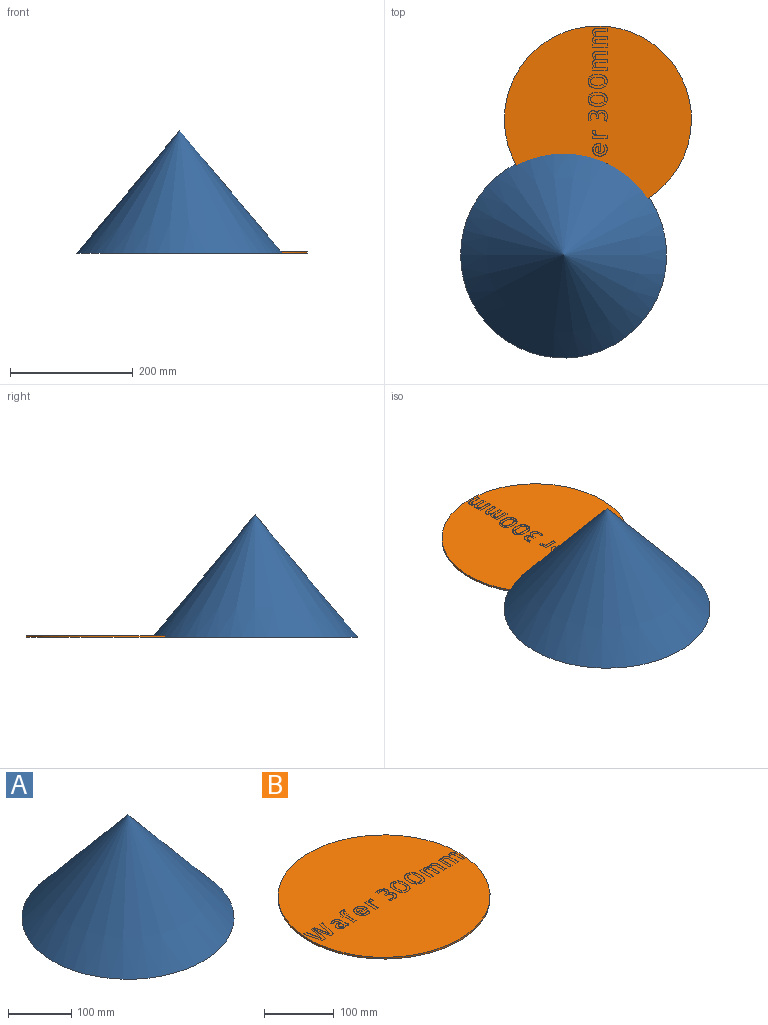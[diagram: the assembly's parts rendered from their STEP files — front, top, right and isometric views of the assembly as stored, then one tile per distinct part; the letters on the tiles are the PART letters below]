
ASSEMBLY  parts=2 mates=1
PART A: 2 faces, bbox 335.6x335.6x200 mm
  f0: plane 335.64x335.64mm, normal (0,0,-1), area 88478.3mm2, adj f1
  f1: cone r=0mm half-angle=40deg, axis (0,0,-1), area 137647.8mm2, adj f0
PART B: 355 faces, bbox 304.8x304.8x3 mm
  f0: plane 304.8x304.8mm, normal (0,0,1), area 70013.2mm2, adj f1,f3,f4,f5,f6,f7,f9,f10
  f1: cylinder r=152.4mm len=304.8mm, axis (0,0,1), area 2872.7mm2, adj f0,f2
  f2: plane 304.8x304.8mm, normal (0,0,-1), area 72965.9mm2, adj f1
  f3: plane 4.49x0.5mm, normal (0,-1,0), area 2.2mm2, adj f0,f4,f7,f8
  f4: plane 23.22x0.5mm, normal (1,0,0), area 11.6mm2, adj f0,f3,f5,f8
  f5: plane 5.02x0.5mm, normal (0,1,0), area 2.5mm2, adj f0,f4,f6,f8
  f6: plane 20.84x0.5mm, normal (-1,0,0), area 10.4mm2, adj f0,f5,f7,f8
  f7: plane 2.38x0.53mm, normal (-0.98,-0.22,0), area 1.2mm2, adj f0,f3,f6,f8
  f8: plane 23.22x5.02mm, normal (0,0,1), area 115.9mm2, adj f3,f4,f5,f6,f7
  f9: extruded ~2.14x0.5mm, area 1.1mm2, adj f0,f10,f24,f25
  f10: extruded ~2.27x1.03mm, area 1.2mm2, adj f0,f9,f11,f25
  f11: plane 3.25x0.5mm, normal (1,0,0), area 1.6mm2, adj f0,f10,f12,f25
  f12: extruded ~2.18x0.7mm, area 1.2mm2, adj f0,f11,f13,f25
  f13: extruded ~1.24x0.5mm, area 0.6mm2, adj f0,f12,f14,f25
  f14: extruded ~1.71x0.55mm, area 0.9mm2, adj f0,f13,f15,f25
  f15: extruded ~1.54x0.8mm, area 0.9mm2, adj f0,f14,f16,f25
  f16: extruded ~2.25x0.5mm, area 1.1mm2, adj f0,f15,f17,f25
  f17: extruded ~2.65x0.5mm, area 1.3mm2, adj f0,f16,f18,f25
  f18: plane 12.64x0.5mm, normal (1,0,0), area 6.3mm2, adj f0,f17,f19,f25
  f19: plane 4.94x0.5mm, normal (0,1,0), area 2.5mm2, adj f0,f18,f20,f25
  f20: plane 15.81x0.5mm, normal (-1,0,0), area 7.9mm2, adj f0,f19,f21,f25
  f21: extruded ~3.07x0.51mm, area 1.6mm2, adj f0,f20,f22,f25
  f22: extruded ~2.45x1.44mm, area 1.4mm2, adj f0,f21,f23,f25
  f23: extruded ~2.16x1.59mm, area 1.4mm2, adj f0,f22,f24,f25
  f24: extruded ~2.63x0.56mm, area 1.4mm2, adj f0,f9,f23,f25
  f25: plane 23.47x11.16mm, normal (0,0,1), area 130mm2, adj f9,f10,f11,f12,f13,f14,f15,f16
  f26: extruded ~2.54x2.31mm, area 1.7mm2, adj f0,f27,f43,f44
  f27: extruded ~3.19x0.78mm, area 1.7mm2, adj f0,f26,f28,f44
  f28: extruded ~2.25x0.5mm, area 1.1mm2, adj f0,f27,f29,f44
  f29: extruded ~2.12x0.95mm, area 1.2mm2, adj f0,f28,f30,f44
  f30: plane 3.25x0.5mm, normal (1,0,0), area 1.6mm2, adj f0,f29,f31,f44
  f31: extruded ~1.92x0.64mm, area 1mm2, adj f0,f30,f32,f44
  f32: extruded ~1.46x0.5mm, area 0.7mm2, adj f0,f31,f33,f44
  f33: extruded ~1.69x0.55mm, area 0.9mm2, adj f0,f32,f34,f44
  f34: extruded ~1.54x0.82mm, area 0.9mm2, adj f0,f33,f35,f44
  f35: extruded ~2.25x0.5mm, area 1.1mm2, adj f0,f34,f36,f44
  f36: plane 2.65x0.5mm, normal (1,0,0), area 1.3mm2, adj f0,f35,f37,f44
  f37: plane 12.64x0.5mm, normal (1,0,0), area 6.3mm2, adj f0,f36,f38,f44
  f38: plane 4.98x0.5mm, normal (0,1,0), area 2.5mm2, adj f0,f37,f39,f44
  f39: plane 13.05x0.5mm, normal (-1,0,0), area 6.5mm2, adj f0,f38,f40,f44
  f40: extruded ~2.04x0.5mm, area 1mm2, adj f0,f39,f41,f44
  f41: extruded ~1.87x0.5mm, area 0.9mm2, adj f0,f40,f42,f44
  f42: extruded ~1.75x0.5mm, area 0.9mm2, adj f0,f41,f43,f44
  f43: extruded ~1.58x0.72mm, area 0.9mm2, adj f0,f26,f42,f44
  f44: plane 23.38x11.15mm, normal (0,0,1), area 130.7mm2, adj f26,f27,f28,f29,f30,f31,f32,f33
  f45: extruded ~3.04x0.87mm, area 1.6mm2, adj f0,f46,f60,f61
  f46: plane 3.87x1.81mm, normal (-0.91,0.42,0), area 2.1mm2, adj f0,f45,f47,f61
  f47: extruded ~4.98x1.07mm, area 2.6mm2, adj f0,f46,f48,f61
  f48: extruded ~4.84x1.01mm, area 2.5mm2, adj f0,f47,f49,f61
  f49: extruded ~3.67x2.94mm, area 2.4mm2, adj f0,f48,f50,f61
  f50: extruded ~4.84x2.31mm, area 2.7mm2, adj f0,f49,f51,f61
  f51: extruded ~6.73x0.8mm, area 3.4mm2, adj f0,f50,f52,f61
  f52: extruded ~7.51x1.03mm, area 3.8mm2, adj f0,f51,f53,f61
  f53: extruded ~5.04x2.92mm, area 2.9mm2, adj f0,f52,f54,f61
  f54: plane 4.82x2.26mm, normal (-0.91,0.42,0), area 2.7mm2, adj f0,f53,f55,f61
  f55: extruded ~3.29x0.86mm, area 1.7mm2, adj f0,f54,f56,f61
  f56: extruded ~4.45x0.5mm, area 2.2mm2, adj f0,f55,f57,f61
  f57: extruded ~5.35x0.51mm, area 2.7mm2, adj f0,f56,f58,f61
  f58: extruded ~3.56x1.34mm, area 1.9mm2, adj f0,f57,f59,f61
  f59: extruded ~2.1x1.96mm, area 1.5mm2, adj f0,f58,f60,f61
  f60: extruded ~2.76x0.58mm, area 1.4mm2, adj f0,f45,f59,f61
  f61: plane 28.07x16.59mm, normal (0,0,1), area 155.3mm2, adj f45,f46,f47,f48,f49,f50,f51,f52
  f62: plane 4.78x2.27mm, normal (0.9,-0.43,0), area 2.6mm2, adj f0,f63,f78,f79
  f63: extruded ~0.5x0.08mm, area 0mm2, adj f0,f62,f64,f79
  f64: extruded ~3.3x0.95mm, area 1.7mm2, adj f0,f63,f65,f79
  f65: extruded ~4.53x0.5mm, area 2.3mm2, adj f0,f64,f66,f79
  f66: extruded ~5.37x0.51mm, area 2.7mm2, adj f0,f65,f67,f79
  f67: extruded ~3.56x1.34mm, area 1.9mm2, adj f0,f66,f68,f79
  f68: extruded ~2.12x1.96mm, area 1.5mm2, adj f0,f67,f69,f79
  f69: extruded ~2.78x0.6mm, area 1.4mm2, adj f0,f68,f70,f79
  f70: extruded ~3.21x1.03mm, area 1.7mm2, adj f0,f69,f71,f79
  f71: plane 3.91x1.85mm, normal (0.9,-0.43,0), area 2.2mm2, adj f0,f70,f72,f79
  f72: extruded ~5.18x1.15mm, area 2.7mm2, adj f0,f71,f73,f79
  f73: extruded ~4.86x0.99mm, area 2.5mm2, adj f0,f72,f74,f79
  f74: extruded ~3.66x2.92mm, area 2.4mm2, adj f0,f73,f75,f79
  f75: extruded ~4.86x2.33mm, area 2.7mm2, adj f0,f74,f76,f79
  f76: extruded ~6.75x0.8mm, area 3.4mm2, adj f0,f75,f77,f79
  f77: extruded ~7.62x1.05mm, area 3.9mm2, adj f0,f76,f78,f79
  f78: extruded ~5.06x3.07mm, area 3mm2, adj f0,f62,f77,f79
  f79: plane 28.2x16.84mm, normal (0,0,1), area 157.8mm2, adj f62,f63,f64,f65,f66,f67,f68,f69
  f80: extruded ~3.04x0.87mm, area 1.6mm2, adj f0,f81,f95,f96
  f81: plane 3.87x1.81mm, normal (-0.91,0.42,0), area 2.1mm2, adj f0,f80,f82,f96
  f82: extruded ~4.98x1.07mm, area 2.6mm2, adj f0,f81,f83,f96
  f83: extruded ~4.84x1.01mm, area 2.5mm2, adj f0,f82,f84,f96
  f84: extruded ~3.67x2.94mm, area 2.4mm2, adj f0,f83,f85,f96
  f85: extruded ~4.84x2.31mm, area 2.7mm2, adj f0,f84,f86,f96
  f86: extruded ~6.73x0.8mm, area 3.4mm2, adj f0,f85,f87,f96
  f87: extruded ~7.51x1.03mm, area 3.8mm2, adj f0,f86,f88,f96
  f88: extruded ~5.04x2.92mm, area 2.9mm2, adj f0,f87,f89,f96
  f89: plane 4.82x2.26mm, normal (-0.91,0.42,0), area 2.7mm2, adj f0,f88,f90,f96
  f90: extruded ~3.29x0.86mm, area 1.7mm2, adj f0,f89,f91,f96
  f91: extruded ~4.45x0.5mm, area 2.2mm2, adj f0,f90,f92,f96
  f92: extruded ~5.35x0.51mm, area 2.7mm2, adj f0,f91,f93,f96
  f93: extruded ~3.56x1.34mm, area 1.9mm2, adj f0,f92,f94,f96
  f94: extruded ~2.1x1.96mm, area 1.5mm2, adj f0,f93,f95,f96
  f95: extruded ~2.76x0.58mm, area 1.4mm2, adj f0,f80,f94,f96
  f96: plane 28.07x16.59mm, normal (0,0,1), area 155.3mm2, adj f80,f81,f82,f83,f84,f85,f86,f87
  f97: plane 3.34x0.5mm, normal (1,0.01,0), area 1.7mm2, adj f0,f98,f141,f142
  f98: plane 4.16x0.5mm, normal (0,1,0), area 2.1mm2, adj f0,f97,f99,f142
  f99: extruded ~3.75x1.52mm, area 2.1mm2, adj f0,f98,f100,f142
  f100: extruded ~3.75x1.28mm, area 2mm2, adj f0,f99,f101,f142
  f101: extruded ~3.89x1.4mm, area 2.1mm2, adj f0,f100,f102,f142
  f102: extruded ~4.25x1.54mm, area 2.3mm2, adj f0,f101,f103,f142
  f103: extruded ~3.04x0.5mm, area 1.5mm2, adj f0,f102,f104,f142
  f104: extruded ~1.73x0.5mm, area 0.9mm2, adj f0,f103,f105,f142
  f105: extruded ~0.95x0.5mm, area 0.5mm2, adj f0,f104,f106,f142
  f106: extruded ~0.71x0.5mm, area 0.4mm2, adj f0,f105,f107,f142
  f107: plane 3.54x1.11mm, normal (0.95,-0.3,0), area 1.9mm2, adj f0,f106,f108,f142
  f108: extruded ~2.78x0.97mm, area 1.5mm2, adj f0,f107,f109,f142
  f109: extruded ~5.46x0.5mm, area 2.7mm2, adj f0,f108,f110,f142
  f110: extruded ~1.38x0.5mm, area 0.7mm2, adj f0,f109,f111,f142
  f111: extruded ~1.95x0.5mm, area 1mm2, adj f0,f110,f112,f142
  f112: extruded ~2.2x0.89mm, area 1.2mm2, adj f0,f111,f113,f142
  f113: extruded ~2.04x1.59mm, area 1.3mm2, adj f0,f112,f114,f142
  f114: extruded ~2.49x1.5mm, area 1.5mm2, adj f0,f113,f115,f142
  f115: extruded ~3.56x0.6mm, area 1.8mm2, adj f0,f114,f116,f142
  f116: extruded ~2.99x0.58mm, area 1.5mm2, adj f0,f115,f117,f142
  f117: extruded ~2.2x1.44mm, area 1.3mm2, adj f0,f116,f118,f142
  f118: extruded ~1.87x1.4mm, area 1.2mm2, adj f0,f117,f119,f142
  f119: extruded ~1.96x0.62mm, area 1mm2, adj f0,f118,f120,f142
  f120: extruded ~1.6x0.68mm, area 0.9mm2, adj f0,f119,f121,f142
  f121: extruded ~1.56x1.3mm, area 1mm2, adj f0,f120,f122,f142
  f122: extruded ~1.83x1.15mm, area 1.1mm2, adj f0,f121,f123,f142
  f123: extruded ~2.32x0.5mm, area 1.2mm2, adj f0,f122,f124,f142
  f124: extruded ~3.79x0.76mm, area 1.9mm2, adj f0,f123,f125,f142
  f125: extruded ~2.64x2.06mm, area 1.7mm2, adj f0,f124,f126,f142
  f126: extruded ~3.03x1.5mm, area 1.7mm2, adj f0,f125,f127,f142
  f127: extruded ~3.67x0.5mm, area 1.9mm2, adj f0,f126,f128,f142
  f128: extruded ~4.22x0.5mm, area 2.1mm2, adj f0,f127,f129,f142
  f129: extruded ~2.45x0.61mm, area 1.3mm2, adj f0,f128,f130,f142
  f130: plane 3.71x1.44mm, normal (0.93,0.36,0), area 2mm2, adj f0,f129,f131,f142
  f131: extruded ~1.71x0.56mm, area 0.9mm2, adj f0,f130,f132,f142
  f132: extruded ~3.02x0.5mm, area 1.5mm2, adj f0,f131,f133,f142
  f133: extruded ~2.97x0.5mm, area 1.5mm2, adj f0,f132,f134,f142
  f134: extruded ~1.62x1.13mm, area 1mm2, adj f0,f133,f135,f142
  f135: extruded ~1.52x0.68mm, area 0.8mm2, adj f0,f134,f136,f142
  f136: extruded ~1.57x0.5mm, area 0.8mm2, adj f0,f135,f137,f142
  f137: extruded ~2.84x0.54mm, area 1.5mm2, adj f0,f136,f138,f142
  f138: extruded ~1.4x1.36mm, area 1mm2, adj f0,f137,f139,f142
  f139: extruded ~1.75x0.5mm, area 0.9mm2, adj f0,f138,f140,f142
  f140: extruded ~1.83x0.5mm, area 0.9mm2, adj f0,f139,f141,f142
  f141: plane 2.8x0.5mm, normal (0,-1,0), area 1.4mm2, adj f0,f97,f140,f142
  f142: plane 30.71x17.9mm, normal (0,0,1), area 228.3mm2, adj f97,f98,f99,f100,f101,f102,f103,f104
  f143: plane 4.78x2.27mm, normal (0.9,-0.43,0), area 2.6mm2, adj f0,f144,f159,f160
  f144: extruded ~0.5x0.08mm, area 0mm2, adj f0,f143,f145,f160
  f145: extruded ~3.3x0.95mm, area 1.7mm2, adj f0,f144,f146,f160
  f146: extruded ~4.53x0.5mm, area 2.3mm2, adj f0,f145,f147,f160
  f147: extruded ~5.37x0.51mm, area 2.7mm2, adj f0,f146,f148,f160
  f148: extruded ~3.56x1.34mm, area 1.9mm2, adj f0,f147,f149,f160
  f149: extruded ~2.12x1.96mm, area 1.5mm2, adj f0,f148,f150,f160
  f150: extruded ~2.78x0.6mm, area 1.4mm2, adj f0,f149,f151,f160
  f151: extruded ~3.21x1.03mm, area 1.7mm2, adj f0,f150,f152,f160
  f152: plane 3.91x1.85mm, normal (0.9,-0.43,0), area 2.2mm2, adj f0,f151,f153,f160
  f153: extruded ~5.18x1.15mm, area 2.7mm2, adj f0,f152,f154,f160
  f154: extruded ~4.86x0.99mm, area 2.5mm2, adj f0,f153,f155,f160
  f155: extruded ~3.66x2.92mm, area 2.4mm2, adj f0,f154,f156,f160
  f156: extruded ~4.86x2.33mm, area 2.7mm2, adj f0,f155,f157,f160
  f157: extruded ~6.75x0.8mm, area 3.4mm2, adj f0,f156,f158,f160
  f158: extruded ~7.62x1.05mm, area 3.9mm2, adj f0,f157,f159,f160
  f159: extruded ~5.06x3.07mm, area 3mm2, adj f0,f143,f158,f160
  f160: plane 28.2x16.84mm, normal (0,0,1), area 157.8mm2, adj f143,f144,f145,f146,f147,f148,f149,f150
  f161: plane 4.49x0.5mm, normal (0,-1,0), area 2.2mm2, adj f0,f162,f165,f166
  f162: plane 23.22x0.5mm, normal (1,0,0), area 11.6mm2, adj f0,f161,f163,f166
  f163: plane 5.02x0.5mm, normal (0,1,0), area 2.5mm2, adj f0,f162,f164,f166
  f164: plane 20.84x0.5mm, normal (-1,0,0), area 10.4mm2, adj f0,f163,f165,f166
  f165: plane 2.38x0.53mm, normal (-0.98,-0.22,0), area 1.2mm2, adj f0,f161,f164,f166
  f166: plane 23.22x5.02mm, normal (0,0,1), area 115.9mm2, adj f161,f162,f163,f164,f165
  f167: extruded ~2.14x0.5mm, area 1.1mm2, adj f0,f168,f182,f183
  f168: extruded ~2.27x1.03mm, area 1.2mm2, adj f0,f167,f169,f183
  f169: plane 3.25x0.5mm, normal (1,0,0), area 1.6mm2, adj f0,f168,f170,f183
  f170: extruded ~2.18x0.7mm, area 1.2mm2, adj f0,f169,f171,f183
  f171: extruded ~1.24x0.5mm, area 0.6mm2, adj f0,f170,f172,f183
  f172: extruded ~1.71x0.55mm, area 0.9mm2, adj f0,f171,f173,f183
  f173: extruded ~1.54x0.8mm, area 0.9mm2, adj f0,f172,f174,f183
  f174: extruded ~2.25x0.5mm, area 1.1mm2, adj f0,f173,f175,f183
  f175: extruded ~2.65x0.5mm, area 1.3mm2, adj f0,f174,f176,f183
  f176: plane 12.64x0.5mm, normal (1,0,0), area 6.3mm2, adj f0,f175,f177,f183
  f177: plane 4.94x0.5mm, normal (0,1,0), area 2.5mm2, adj f0,f176,f178,f183
  f178: plane 15.81x0.5mm, normal (-1,0,0), area 7.9mm2, adj f0,f177,f179,f183
  f179: extruded ~3.07x0.51mm, area 1.6mm2, adj f0,f178,f180,f183
  f180: extruded ~2.45x1.44mm, area 1.4mm2, adj f0,f179,f181,f183
  f181: extruded ~2.16x1.59mm, area 1.4mm2, adj f0,f180,f182,f183
  f182: extruded ~2.63x0.56mm, area 1.4mm2, adj f0,f167,f181,f183
  f183: plane 23.47x11.16mm, normal (0,0,1), area 130mm2, adj f167,f168,f169,f170,f171,f172,f173,f174
  f184: extruded ~2.54x2.31mm, area 1.7mm2, adj f0,f185,f201,f202
  f185: extruded ~3.19x0.78mm, area 1.7mm2, adj f0,f184,f186,f202
  f186: extruded ~2.25x0.5mm, area 1.1mm2, adj f0,f185,f187,f202
  f187: extruded ~2.12x0.95mm, area 1.2mm2, adj f0,f186,f188,f202
  f188: plane 3.25x0.5mm, normal (1,0,0), area 1.6mm2, adj f0,f187,f189,f202
  f189: extruded ~1.92x0.64mm, area 1mm2, adj f0,f188,f190,f202
  f190: extruded ~1.46x0.5mm, area 0.7mm2, adj f0,f189,f191,f202
  f191: extruded ~1.69x0.55mm, area 0.9mm2, adj f0,f190,f192,f202
  f192: extruded ~1.54x0.82mm, area 0.9mm2, adj f0,f191,f193,f202
  f193: extruded ~2.25x0.5mm, area 1.1mm2, adj f0,f192,f194,f202
  f194: plane 2.65x0.5mm, normal (1,0,0), area 1.3mm2, adj f0,f193,f195,f202
  f195: plane 12.64x0.5mm, normal (1,0,0), area 6.3mm2, adj f0,f194,f196,f202
  f196: plane 4.98x0.5mm, normal (0,1,0), area 2.5mm2, adj f0,f195,f197,f202
  f197: plane 13.05x0.5mm, normal (-1,0,0), area 6.5mm2, adj f0,f196,f198,f202
  f198: extruded ~2.04x0.5mm, area 1mm2, adj f0,f197,f199,f202
  f199: extruded ~1.87x0.5mm, area 0.9mm2, adj f0,f198,f200,f202
  f200: extruded ~1.75x0.5mm, area 0.9mm2, adj f0,f199,f201,f202
  f201: extruded ~1.58x0.72mm, area 0.9mm2, adj f0,f184,f200,f202
  f202: plane 23.38x11.15mm, normal (0,0,1), area 130.7mm2, adj f184,f185,f186,f187,f188,f189,f190,f191
  f203: plane 4.2x0.5mm, normal (1,0,0), area 2.1mm2, adj f0,f204,f209,f210
  f204: extruded ~1.75x0.5mm, area 0.9mm2, adj f0,f203,f205,f210
  f205: extruded ~1.83x0.5mm, area 0.9mm2, adj f0,f204,f206,f210
  f206: extruded ~2.8x0.5mm, area 1.4mm2, adj f0,f205,f207,f210
  f207: plane 5.18x0.5mm, normal (-1,0,0), area 2.6mm2, adj f0,f206,f208,f210
  f208: extruded ~3.91x0.5mm, area 2mm2, adj f0,f207,f209,f210
  f209: extruded ~2.47x0.88mm, area 1.3mm2, adj f0,f203,f208,f210
  f210: plane 6.38x5.4mm, normal (0,0,1), area 29.7mm2, adj f203,f204,f205,f206,f207,f208,f209
  f211: plane 4.45x0.5mm, normal (0,-1,0), area 2.2mm2, adj f0,f212,f215,f216
  f212: plane 23.22x0.5mm, normal (1,0,0), area 11.6mm2, adj f0,f211,f213,f216
  f213: plane 4.98x0.5mm, normal (0,1,0), area 2.5mm2, adj f0,f212,f214,f216
  f214: plane 20.84x0.5mm, normal (-1,0,0), area 10.4mm2, adj f0,f213,f215,f216
  f215: plane 2.38x0.53mm, normal (-0.98,-0.22,0), area 1.2mm2, adj f0,f211,f214,f216
  f216: plane 23.22x4.98mm, normal (0,0,1), area 115mm2, adj f211,f212,f213,f214,f215
  f217: plane 3.87x0.5mm, normal (1,0,0), area 1.9mm2, adj f0,f218,f229,f230
  f218: extruded ~2.02x0.7mm, area 1.1mm2, adj f0,f217,f219,f230
  f219: extruded ~1.58x1.42mm, area 1.1mm2, adj f0,f218,f220,f230
  f220: extruded ~1.83x1.03mm, area 1.1mm2, adj f0,f219,f221,f230
  f221: extruded ~2.06x0.5mm, area 1.1mm2, adj f0,f220,f222,f230
  f222: plane 9.51x0.5mm, normal (0,-1,0), area 4.8mm2, adj f0,f221,f223,f230
  f223: plane 3.62x0.5mm, normal (1,0,0), area 1.8mm2, adj f0,f222,f224,f230
  f224: plane 14.12x0.5mm, normal (0,1,0), area 7.1mm2, adj f0,f223,f225,f230
  f225: extruded ~1.98x0.5mm, area 1mm2, adj f0,f224,f226,f230
  f226: extruded ~4.2x0.68mm, area 2.1mm2, adj f0,f225,f227,f230
  f227: extruded ~3.58x1.96mm, area 2.1mm2, adj f0,f226,f228,f230
  f228: extruded ~3.07x2.55mm, area 2mm2, adj f0,f227,f229,f230
  f229: extruded ~4.02x1.19mm, area 2.1mm2, adj f0,f217,f228,f230
  f230: plane 14.24x13.5mm, normal (0,0,1), area 99.8mm2, adj f217,f218,f219,f220,f221,f222,f223,f224
  f231: extruded ~2.94x0.6mm, area 1.5mm2, adj f0,f232,f254,f255
  f232: extruded ~2.04x1.6mm, area 1.3mm2, adj f0,f231,f233,f255
  f233: extruded ~2.39x1.22mm, area 1.3mm2, adj f0,f232,f234,f255
  f234: extruded ~2.99x0.5mm, area 1.5mm2, adj f0,f233,f235,f255
  f235: extruded ~2.18x0.5mm, area 1.1mm2, adj f0,f234,f236,f255
  f236: extruded ~2.49x0.78mm, area 1.3mm2, adj f0,f235,f237,f255
  f237: extruded ~2.16x1.54mm, area 1.3mm2, adj f0,f236,f238,f255
  f238: extruded ~2.51x1.24mm, area 1.4mm2, adj f0,f237,f239,f255
  f239: plane 3.95x0.5mm, normal (-1,0,0), area 2mm2, adj f0,f238,f240,f255
  f240: extruded ~3.77x1.11mm, area 2mm2, adj f0,f239,f241,f255
  f241: extruded ~3.07x2.57mm, area 2mm2, adj f0,f240,f242,f255
  f242: extruded ~3.69x2.08mm, area 2.1mm2, adj f0,f241,f243,f255
  f243: extruded ~4.45x0.76mm, area 2.3mm2, adj f0,f242,f244,f255
  f244: extruded ~4.61x0.82mm, area 2.4mm2, adj f0,f243,f245,f255
  f245: extruded ~3.75x2.22mm, area 2.2mm2, adj f0,f244,f246,f255
  f246: extruded ~3.38x2.53mm, area 2.1mm2, adj f0,f245,f247,f255
  f247: extruded ~4.24x0.93mm, area 2.2mm2, adj f0,f246,f248,f255
  f248: extruded ~4.61x0.87mm, area 2.4mm2, adj f0,f247,f249,f255
  f249: extruded ~3.17x2.55mm, area 2.1mm2, adj f0,f248,f250,f255
  f250: plane 2.76x1.81mm, normal (-0.84,-0.55,0), area 1.7mm2, adj f0,f249,f251,f255
  f251: extruded ~1.34x0.99mm, area 0.8mm2, adj f0,f250,f252,f255
  f252: extruded ~1.53x0.68mm, area 0.8mm2, adj f0,f251,f253,f255
  f253: extruded ~1.44x0.5mm, area 0.7mm2, adj f0,f252,f254,f255
  f254: extruded ~1.13x0.5mm, area 0.6mm2, adj f0,f231,f253,f255
  f255: plane 23.63x18.44mm, normal (0,0,1), area 148.8mm2, adj f231,f232,f233,f234,f235,f236,f237,f238
  f256: plane 26.18x5.81mm, normal (0.98,-0.22,0), area 13.4mm2, adj f0,f257,f263,f264
  f257: plane 26.18x5.35mm, normal (-0.98,-0.2,0), area 13.4mm2, adj f0,f256,f258,f264
  f258: plane 1.98x0.5mm, normal (0,-1,0), area 1mm2, adj f0,f257,f259,f264
  f259: plane 11.77x0.5mm, normal (1,0,0), area 5.9mm2, adj f0,f258,f260,f264
  f260: plane 18.73x4.12mm, normal (0.98,0.21,0), area 9.6mm2, adj f0,f259,f261,f264
  f261: plane 6.42x0.5mm, normal (0,1,0), area 3.2mm2, adj f0,f260,f262,f264
  f262: plane 30.51x8.19mm, normal (-0.97,0.26,0), area 15.8mm2, adj f0,f261,f263,f264
  f263: plane 5.6x0.5mm, normal (0,-1,0), area 2.8mm2, adj f0,f256,f262,f264
  f264: plane 30.51x18.73mm, normal (0,0,1), area 261.8mm2, adj f256,f257,f258,f259,f260,f261,f262,f263
  f265: extruded ~2.16x0.51mm, area 1.1mm2, adj f0,f266,f283,f284
  f266: extruded ~1.3x1.29mm, area 0.9mm2, adj f0,f265,f267,f284
  f267: extruded ~1.69x0.62mm, area 0.9mm2, adj f0,f266,f268,f284
  f268: extruded ~1.73x0.5mm, area 0.9mm2, adj f0,f267,f269,f284
  f269: plane 0.9x0.5mm, normal (0,1,0), area 0.5mm2, adj f0,f268,f270,f284
  f270: plane 2.92x0.5mm, normal (-1,0,0), area 1.5mm2, adj f0,f269,f271,f284
  f271: plane 1.81x0.5mm, normal (0,-1,0), area 0.9mm2, adj f0,f270,f272,f284
  f272: extruded ~3.25x0.5mm, area 1.6mm2, adj f0,f271,f273,f284
  f273: extruded ~2.86x1.32mm, area 1.6mm2, adj f0,f272,f274,f284
  f274: extruded ~2.27x2.06mm, area 1.5mm2, adj f0,f273,f275,f284
  f275: extruded ~3.27x0.8mm, area 1.7mm2, adj f0,f274,f276,f284
  f276: extruded ~3.34x0.56mm, area 1.7mm2, adj f0,f275,f277,f284
  f277: extruded ~2.18x1.54mm, area 1.4mm2, adj f0,f276,f278,f284
  f278: extruded ~2.28x1.19mm, area 1.3mm2, adj f0,f277,f279,f284
  f279: extruded ~2.7x0.5mm, area 1.4mm2, adj f0,f278,f280,f284
  f280: extruded ~0.53x0.5mm, area 0.3mm2, adj f0,f279,f281,f284
  f281: plane 3.33x0.5mm, normal (-1,0,0), area 1.7mm2, adj f0,f280,f282,f284
  f282: extruded ~2.2x1.07mm, area 1.3mm2, adj f0,f281,f283,f284
  f283: extruded ~2.76x0.76mm, area 1.5mm2, adj f0,f265,f282,f284
  f284: plane 14.37x10.78mm, normal (0,0,1), area 79.2mm2, adj f265,f266,f267,f268,f269,f270,f271,f272
  f285: plane 5.68x0.5mm, normal (-1,0,0), area 2.8mm2, adj f0,f286,f319,f320
  f286: extruded ~2.91x0.5mm, area 1.5mm2, adj f0,f285,f287,f320
  f287: extruded ~2.91x0.5mm, area 1.5mm2, adj f0,f286,f288,f320
  f288: extruded ~2.4x1.01mm, area 1.3mm2, adj f0,f287,f289,f320
  f289: extruded ~1.69x1.54mm, area 1.2mm2, adj f0,f288,f290,f320
  f290: extruded ~2.14x0.82mm, area 1.2mm2, adj f0,f289,f291,f320
  f291: extruded ~2.41x0.5mm, area 1.2mm2, adj f0,f290,f292,f320
  f292: extruded ~2.62x0.5mm, area 1.3mm2, adj f0,f291,f293,f320
  f293: extruded ~2.33x0.6mm, area 1.2mm2, adj f0,f292,f294,f320
  f294: extruded ~1.89x0.84mm, area 1mm2, adj f0,f293,f295,f320
  f295: extruded ~1.23x0.93mm, area 0.8mm2, adj f0,f294,f296,f320
  f296: plane 2.84x1.85mm, normal (0.84,0.55,0), area 1.7mm2, adj f0,f295,f297,f320
  f297: extruded ~0.76x0.58mm, area 0.5mm2, adj f0,f296,f298,f320
  f298: extruded ~1.19x0.68mm, area 0.7mm2, adj f0,f297,f299,f320
  f299: extruded ~1.48x0.53mm, area 0.8mm2, adj f0,f298,f300,f320
  f300: extruded ~1.71x0.5mm, area 0.9mm2, adj f0,f299,f301,f320
  f301: extruded ~1.71x0.5mm, area 0.9mm2, adj f0,f300,f302,f320
  f302: extruded ~1.22x0.7mm, area 0.7mm2, adj f0,f301,f303,f320
  f303: extruded ~1.75x0.7mm, area 1mm2, adj f0,f302,f304,f320
  f304: extruded ~3.21x0.5mm, area 1.6mm2, adj f0,f303,f305,f320
  f305: plane 8.69x0.5mm, normal (1,0,0), area 4.3mm2, adj f0,f304,f306,f320
  f306: extruded ~1.42x1.38mm, area 1mm2, adj f0,f305,f307,f320
  f307: extruded ~1.79x0.8mm, area 1mm2, adj f0,f306,f308,f320
  f308: plane 3.13x0.5mm, normal (1,0,0), area 1.6mm2, adj f0,f307,f309,f320
  f309: extruded ~2.7x1.17mm, area 1.5mm2, adj f0,f308,f310,f320
  f310: extruded ~1.83x1.63mm, area 1.2mm2, adj f0,f309,f311,f320
  f311: extruded ~1.22x0.6mm, area 0.7mm2, adj f0,f310,f312,f320
  f312: extruded ~1.01x0.95mm, area 0.7mm2, adj f0,f311,f313,f320
  f313: extruded ~1.15x0.7mm, area 0.7mm2, adj f0,f312,f314,f320
  f314: extruded ~1.13x0.5mm, area 0.6mm2, adj f0,f313,f315,f320
  f315: plane 2.76x1.32mm, normal (-0.9,0.43,0), area 1.5mm2, adj f0,f314,f316,f320
  f316: extruded ~0.72x0.7mm, area 0.5mm2, adj f0,f315,f317,f320
  f317: extruded ~1.19x0.5mm, area 0.6mm2, adj f0,f316,f318,f320
  f318: extruded ~1.3x0.5mm, area 0.7mm2, adj f0,f317,f319,f320
  f319: extruded ~0.97x0.5mm, area 0.5mm2, adj f0,f285,f318,f320
  f320: plane 23.42x17.13mm, normal (0,0,1), area 150.3mm2, adj f285,f286,f287,f288,f289,f290,f291,f292
  f321: extruded ~1.13x0.5mm, area 0.6mm2, adj f0,f322,f344,f345
  f322: extruded ~1.38x0.5mm, area 0.7mm2, adj f0,f321,f323,f345
  f323: plane 2.96x1.61mm, normal (-0.88,0.48,0), area 1.7mm2, adj f0,f322,f324,f345
  f324: extruded ~0.91x0.5mm, area 0.5mm2, adj f0,f323,f325,f345
  f325: extruded ~1.26x0.5mm, area 0.7mm2, adj f0,f324,f326,f345
  f326: extruded ~1.38x0.5mm, area 0.7mm2, adj f0,f325,f327,f345
  f327: extruded ~1.32x0.5mm, area 0.7mm2, adj f0,f326,f328,f345
  f328: extruded ~3.47x0.74mm, area 1.8mm2, adj f0,f327,f329,f345
  f329: extruded ~2.18x1.95mm, area 1.5mm2, adj f0,f328,f330,f345
  f330: extruded ~2.84x1.17mm, area 1.5mm2, adj f0,f329,f331,f345
  f331: extruded ~3.4x0.5mm, area 1.7mm2, adj f0,f330,f332,f345
  f332: plane 3.13x0.5mm, normal (0,-1,0), area 1.6mm2, adj f0,f331,f333,f345
  f333: plane 3.37x0.5mm, normal (1,0,0), area 1.7mm2, adj f0,f332,f334,f345
  f334: plane 3.04x0.5mm, normal (0,1,0), area 1.5mm2, adj f0,f333,f335,f345
  f335: plane 19.85x0.5mm, normal (1,0,0), area 9.9mm2, adj f0,f334,f336,f345
  f336: plane 5.03x0.5mm, normal (0,1,0), area 2.5mm2, adj f0,f335,f337,f345
  f337: plane 19.85x0.5mm, normal (-1,0,0), area 9.9mm2, adj f0,f336,f338,f345
  f338: plane 3.66x0.5mm, normal (0,1,0), area 1.8mm2, adj f0,f337,f339,f345
  f339: plane 3.37x0.5mm, normal (-1,0,0), area 1.7mm2, adj f0,f338,f340,f345
  f340: plane 3.58x0.5mm, normal (0,-1,0), area 1.8mm2, adj f0,f339,f341,f345
  f341: extruded ~2.04x0.5mm, area 1mm2, adj f0,f340,f342,f345
  f342: extruded ~1.71x0.53mm, area 0.9mm2, adj f0,f341,f343,f345
  f343: extruded ~1.15x0.93mm, area 0.7mm2, adj f0,f342,f344,f345
  f344: extruded ~1.38x0.5mm, area 0.7mm2, adj f0,f321,f343,f345
  f345: plane 32.15x15.32mm, normal (0,0,1), area 198mm2, adj f321,f322,f323,f324,f325,f326,f327,f328
  f346: plane 26.18x5.36mm, normal (-0.98,-0.2,0), area 13.4mm2, adj f0,f347,f353,f354
  f347: plane 5.6x0.5mm, normal (0,-1,0), area 2.8mm2, adj f0,f346,f348,f354
  f348: plane 30.51x7.7mm, normal (0.97,0.24,0), area 15.7mm2, adj f0,f347,f349,f354
  f349: plane 6.46x0.5mm, normal (0,1,0), area 3.2mm2, adj f0,f348,f350,f354
  f350: plane 19.52x4.49mm, normal (-0.97,0.22,0), area 10mm2, adj f0,f349,f351,f354
  f351: plane 10.99x0.5mm, normal (-1,0,0), area 5.5mm2, adj f0,f350,f352,f354
  f352: plane 1.94x0.5mm, normal (0,-1,0), area 1mm2, adj f0,f351,f353,f354
  f353: plane 26.18x5.76mm, normal (0.98,-0.21,0), area 13.4mm2, adj f0,f346,f352,f354
  f354: plane 30.51x18.65mm, normal (0,0,1), area 262.2mm2, adj f346,f347,f348,f349,f350,f351,f352,f353
PLACE A t=(-55.56,-216.42,-42)mm
PLACE B rot(axis=(0,0,1),90deg) t=(0.31,4.41,-39)mm
MATE planar B.f1 <-> A.f1  axis (0,0,1) through (0.31,4.41,-42)mm
